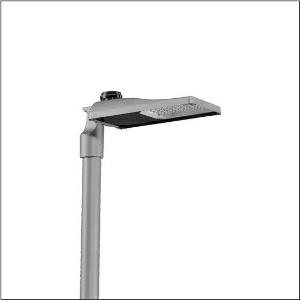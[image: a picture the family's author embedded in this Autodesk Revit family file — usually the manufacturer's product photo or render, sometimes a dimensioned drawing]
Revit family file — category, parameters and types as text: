
# Revit family: streetlight_sl_31_mini___st1_0a_5xh6d3bn08ga_df69
name_source: partatom
category: Lighting Fixtures
units: mm (PartAtom-declared; Revit-internal decimal feet)

## family parameters
Cut with Voids When Loaded = No
Host = Face
Light Source = No
Part Type = Normal
Room Calculation Point = No
Round Connector Dimension = Use Diameter
Shared = No

## types (1)
- --- (1 x LED, 5710 lm, 37.3 W, 3000K)
    Apparent Load = 37 VA
    CIE Flux Codes = 37 72 97 100 100
    Color Rendering = 70
    Color Temperature = 3000K
    Default Elevation = 1800 mm
    Description = Streetlight SL 31 mini NEMA (7pin) mast luminaire for post-top, side-entry; light control with lens of PMMA; light distribution: ST1.0a, direct asymmetric distribution, for standard-compliant lighting for roads and squares; LED: luminous flux: 5.710lm, light colour: 730, colour temperature: 3000K; luminous efficacy: 153,1lm/W; control: pre-setting: linear dimming characteristic, flexible luminous flux parameterisation, time-dependent luminous flux control, constant luminous flux control, intelligent temperature release in ECG and LED module, overheat protection; luminaire housing, of diecast aluminium, Siteco® metallic grey (DB 702S), corrosivity category C5 high according to DIN EN ISO 12944; cover of toughened safety glass, transparent, opened without tools; mast flange of diecast aluminium, Siteco® metallic grey (DB 702S), spigot size: 76/60mm, mast flange included unmounted; with cable H07RN-F 3x 1.5mm², cable length: 6,5m, connection cable pre-assembled; mains connection: 220..240V, AC, 50/60Hz; power consumption (at start of service life): 37,3W / (at end of service life): 38,7W / (with reduced operation 50%): 17,5W; protection rating (complete): IP66; insulation class (complete): insulation class I (protective earthing); impact resistance: IK10; certification: CE, ENEC, ENEC+, VDE, UKCA; permissible operating ambient temperature for outdoor applications: -40..+50°C; packaging unit: 1 piece

Light Distribution: ST1.0a
    Height = 76 mm
    Lamp = 1 x LED
    Lamp Light Flux = 5710 lm
    Lamp Power = 37.3 W
    Lamp count = 1
    Length = 547 mm
    Luminous efficacy = 153 lm/W
    Manufacturer = Siteco
    ModVariant = No
    Model = 5XH6D3BN08GA
    Number of Poles = 1
    OnlyDefault = Yes
    Power Factor = 1
    Product Name = Streetlight SL 31 mini | ST1.0a
    Product group = mast luminaire | pylon top
    ProductGroupID = 6100
    Protection Class = Protection class I
    Protection Degree = IP 66
    RLX_Detail_Level = 1
    RLX_Emergency_Light_Flux = 0 lm
    RLX_Emergency_Type = 0
    RLX_Emergency_Type_DB = No
    RlxData = <blob elided: 40137 chars, md5=6115a760>
    Socket = socket
    Standby Power = 0 W
    System Light Flux = 5710 lm
    System Power = 37 W
    Type Comments = factory setting: luminous flux: 100 % | dim-lin: 254 | 386 mA
    Type Image = l_1300322.jpg
    URL = http://relux.com
    VarID = @adj_074187
    Voltage = 0 V
    Weight = 0.00 kg
    Width = 265 mm

## geometry (parser evidence)
native form markers: Blend x4, Sweep x7
no freeform markers — native parametric forms only
